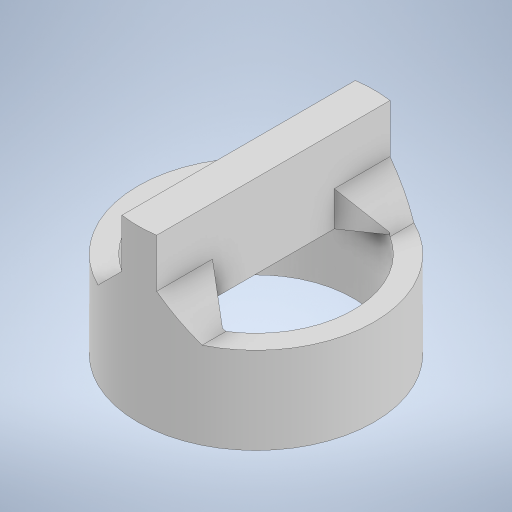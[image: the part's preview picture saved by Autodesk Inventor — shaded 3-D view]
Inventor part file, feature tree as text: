
AUTODESK INVENTOR PART (.ipt)
format: ipt  version: 2024 (Build 280153000, 153)  size: 244,224 bytes
history: native  units: mm
features: extrude x2, chamfer x2, other x1
ambient origin geometry x8: Origin, YZ Plane, XZ Plane, XY Plane, X Axis, Y Axis, Z Axis, Center Point
bodies: Body1 (feature_tree)
feature tree (5):
  other  "솔리드1"
  extrude  "돌출1"  Depth=5.6mm
  extrude  "돌출2"  Depth=6.8mm
  chamfer  "모따기1"  Distance=2.5mm
  chamfer  "모따기2"  Distance=1.0mm
